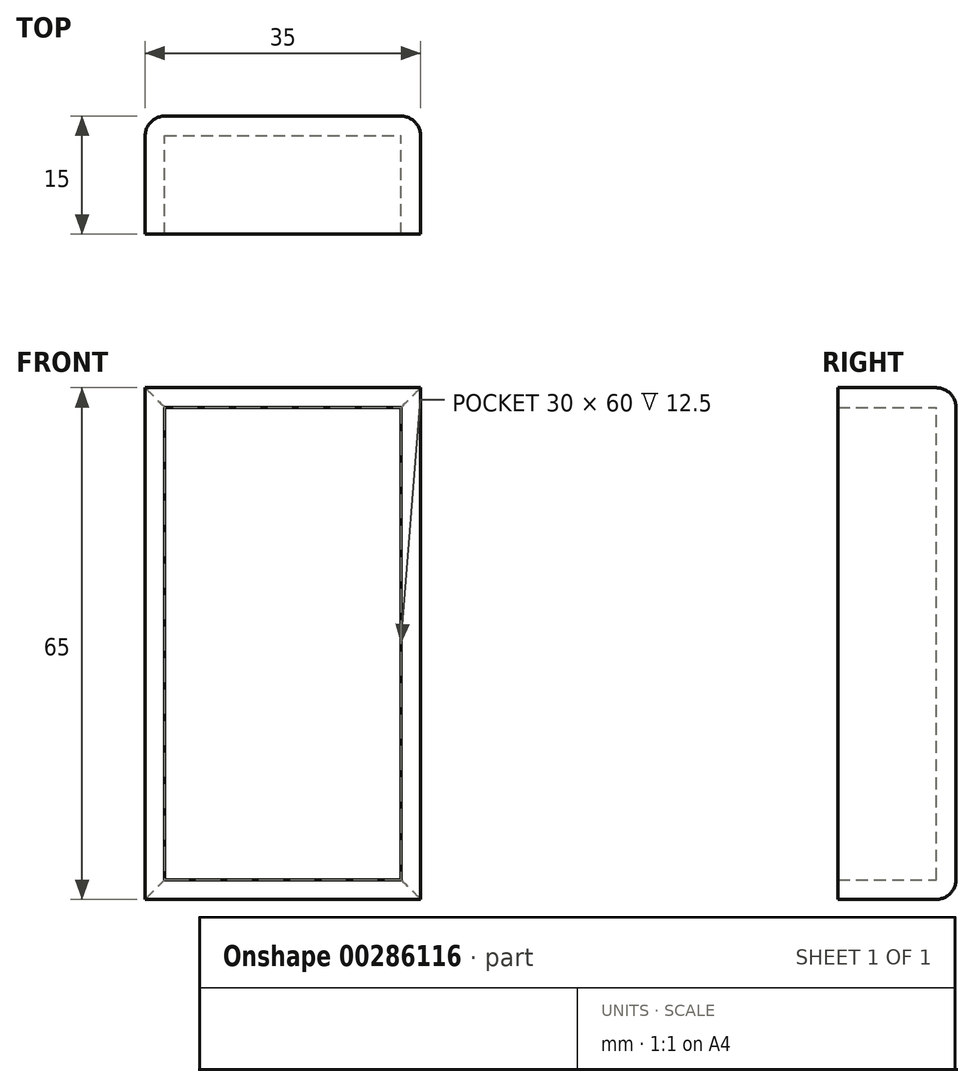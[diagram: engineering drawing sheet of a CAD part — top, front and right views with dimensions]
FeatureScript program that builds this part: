
annotation { "Feature Type Name" : "Feature", "Feature Type Description" : "" }
export const myFeature = defineFeature(function(context is Context, id is Id, definition is map)
    precondition{}
    {
        {
            var Q0;
            Q0=qCreatedBy(makeId("Front.planeOp"),FACE);
            var sketch = newSketch(context, id + "F0", { "sketchPlane" : qUnion([Q0])});
            skLineSegment(sketch, "E0.bottom", {"start": v(0, 0) * mm, "end": v(35, 0) * mm});
            skLineSegment(sketch, "E0.top", {"start": v(0, 65) * mm, "end": v(35, 65) * mm});
            skLineSegment(sketch, "E0.left", {"start": v(0, 0) * mm, "end": v(0, 65) * mm});
            skLineSegment(sketch, "E0.right", {"start": v(35, 0) * mm, "end": v(35, 65) * mm});
            skSolve(sketch);
        }
        {
            var Q0;
            Q0=makeQuery(id+"F0.imprint","IMPRINT",FACE,{"disambiguationData":[TD([[makeQuery(id+"F0.imprint","IMPRINT",EDGE,{"derivedFrom":sQuery(id+"F0.wireOp",EDGE,"E0.bottom")}),1.0]])]});
            extrude(context, id + "F1", {"entities" : qUnion([Q0]), "depth" : 15 * mm});
        }
        {
            var Q0;
            Q0=makeQuery(id+"F1.opExtrude","CAP_FACE",FACE,{"disambiguationData":[OSD([sQuery(id+"F0.wireOp",EDGE,"E0.bottom"),sQuery(id+"F0.wireOp",EDGE,"E0.top"),sQuery(id+"F0.wireOp",EDGE,"E0.left"),sQuery(id+"F0.wireOp",EDGE,"E0.right")])],"isStart":false});
            shell(context, id + "F2", {"entities" : qUnion([Q0]), "thickness" : 2.5 * mm});
        }
        {
            var Q0;
            Q0=makeQuery(id+"F1.opExtrude","CAP_FACE",FACE,{"disambiguationData":[OSD([sQuery(id+"F0.wireOp",EDGE,"E0.bottom"),sQuery(id+"F0.wireOp",EDGE,"E0.top"),sQuery(id+"F0.wireOp",EDGE,"E0.left"),sQuery(id+"F0.wireOp",EDGE,"E0.right")])],"isStart":true});
            fillet(context, id + "F3", {"entities" : qUnion([Q0]), "radius" : 2.5 * mm, "tangentPropagation" : true, "allowEdgeOverflow" : false});
        }
    });
